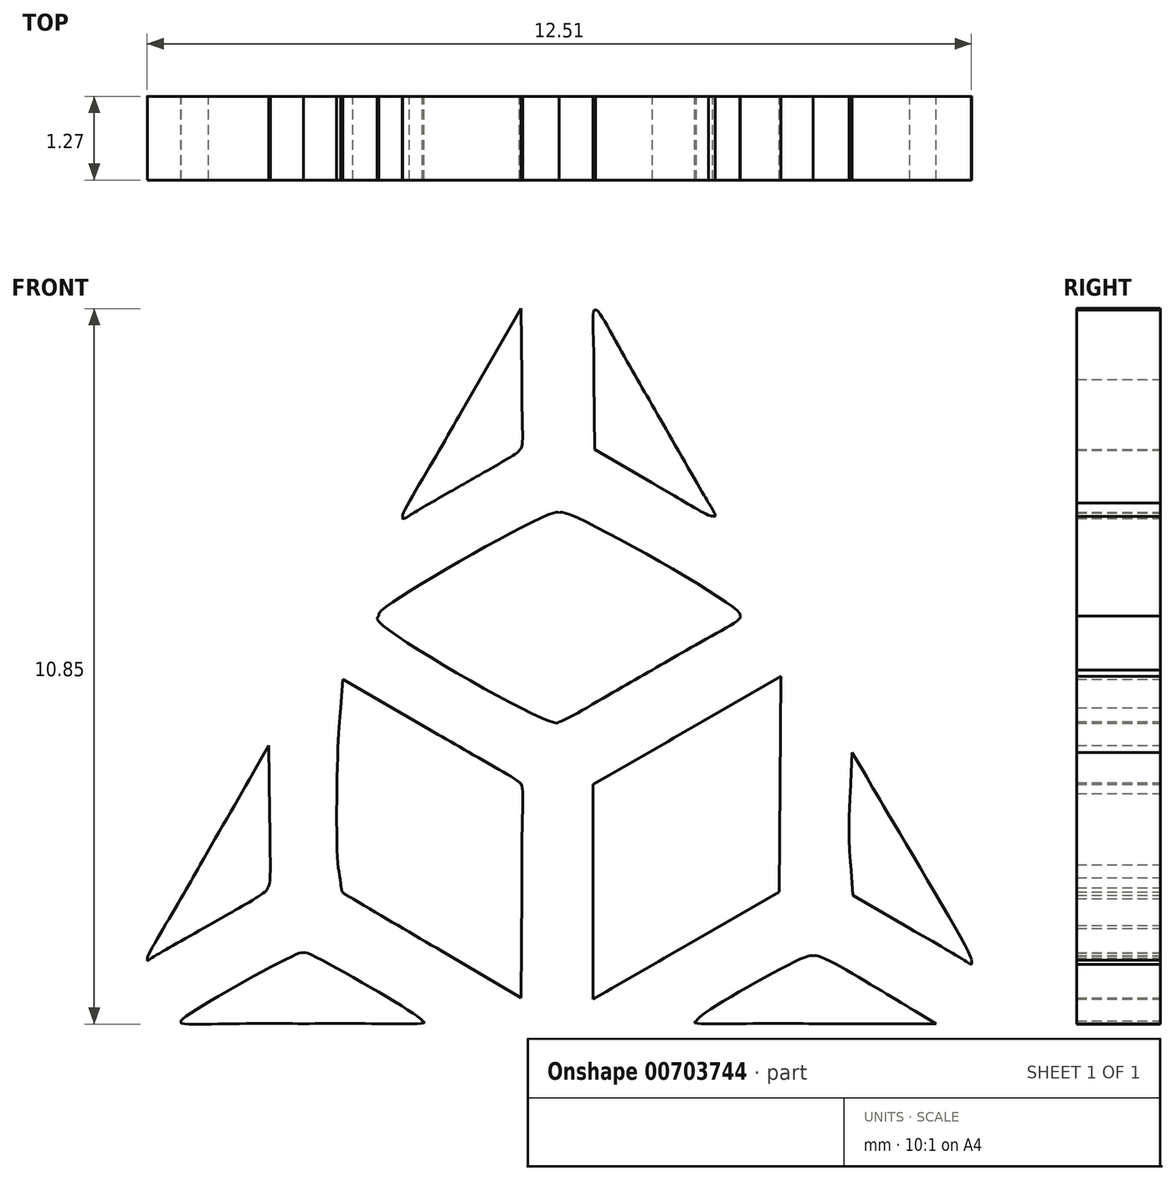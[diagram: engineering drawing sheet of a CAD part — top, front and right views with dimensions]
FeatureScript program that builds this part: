
annotation { "Feature Type Name" : "Feature", "Feature Type Description" : "" }
export const myFeature = defineFeature(function(context is Context, id is Id, definition is map)
    precondition{}
    {
        {
            var Q0;
            Q0=qCreatedBy(makeId("Front.planeOp"),FACE);
            var sketch = newSketch(context, id + "F0", { "sketchPlane" : qUnion([Q0])});
            skFitSpline(sketch, "E0", {"points": [v(-7.56, -9.6) * mm, v(-7.82, -9.54) * mm, v(-7.9, -9.44) * mm, v(-7.9, -9.18) * mm]});
            skFitSpline(sketch, "E1", {"points": [v(-7.9, -9.18) * mm, v(-7.89, -8.9) * mm, v(-8.03, -9.18) * mm, v(-5.89, -5.46) * mm]});
            skFitSpline(sketch, "E2", {"points": [v(-5.89, -5.46) * mm, v(-4.98, -3.9) * mm, v(-3.48, -1.3) * mm, v(-2.55, 0.32) * mm]});
            skFitSpline(sketch, "E3", {"points": [v(-2.55, 0.32) * mm, v(0.18, 5.07) * mm, v(0.04, 4.84) * mm, v(0.3, 4.9) * mm]});
            skFitSpline(sketch, "E4", {"points": [v(0.3, 4.9) * mm, v(0.37, 4.9) * mm, v(0.5, 4.9) * mm, v(0.57, 4.87) * mm]});
            skFitSpline(sketch, "E5", {"points": [v(0.57, 4.87) * mm, v(0.72, 4.82) * mm, v(0.6, 5.03) * mm, v(4.94, -2.5) * mm]});
            skFitSpline(sketch, "E6", {"points": [v(4.94, -2.5) * mm, v(8.66, -8.94) * mm, v(8.66, -8.95) * mm, v(8.68, -9.15) * mm]});
            skFitSpline(sketch, "E7", {"points": [v(8.68, -9.15) * mm, v(8.7, -9.4) * mm, v(8.64, -9.53) * mm, v(8.42, -9.59) * mm]});
            skFitSpline(sketch, "E8", {"points": [v(8.42, -9.59) * mm, v(8.22, -9.64) * mm, v(-7.27, -9.65) * mm, v(-7.56, -9.6) * mm]});
            skFitSpline(sketch, "E9", {"points": [v(-1.7, -8.52) * mm, v(-1.77, -8.45) * mm, v(-3.45, -7.5) * mm, v(-3.5, -7.5) * mm]});
            skFitSpline(sketch, "E10", {"points": [v(-3.5, -7.5) * mm, v(-3.55, -7.5) * mm, v(-5.35, -8.52) * mm, v(-5.35, -8.55) * mm]});
            skFitSpline(sketch, "E11", {"points": [v(-5.35, -8.55) * mm, v(-5.35, -8.56) * mm, v(-4.52, -8.56) * mm, v(-3.5, -8.56) * mm]});
            skFitSpline(sketch, "E12", {"points": [v(-3.5, -8.56) * mm, v(-2.41, -8.56) * mm, v(-1.67, -8.55) * mm, v(-1.7, -8.52) * mm]});
            skLineSegment(sketch, "E13", {"start": v(-7.56, -9.6) * mm, "end": v(-7.56, -9.6) * mm});
            skFitSpline(sketch, "E14", {"points": [v(5.85, -8.4) * mm, v(5.13, -7.98) * mm, v(4.32, -7.54) * mm, v(4.24, -7.54) * mm]});
            skFitSpline(sketch, "E15", {"points": [v(4.24, -7.54) * mm, v(4.16, -7.54) * mm, v(2.58, -8.42) * mm, v(2.47, -8.52) * mm]});
            skFitSpline(sketch, "E16", {"points": [v(2.47, -8.52) * mm, v(2.44, -8.55) * mm, v(3.17, -8.56) * mm, v(4.26, -8.56) * mm]});
            skFitSpline(sketch, "E17", {"points": [v(-0.22, -4.9) * mm, v(-0.24, -4.88) * mm, v(-0.86, -4.52) * mm, v(-1.58, -4.1) * mm]});
            skLineSegment(sketch, "E18", {"start": v(4.26, -8.56) * mm, "end": v(6.1, -8.56) * mm});
            skLineSegment(sketch, "E19", {"start": v(6.1, -8.56) * mm, "end": v(5.85, -8.4) * mm});
            skLineSegment(sketch, "E20", {"start": v(5.85, -8.4) * mm, "end": v(5.85, -8.4) * mm});
            skFitSpline(sketch, "E21", {"points": [v(-2.93, -3.77) * mm, v(-2.97, -4.36) * mm, v(-2.98, -6.07) * mm, v(-2.94, -6.35) * mm]});
            skFitSpline(sketch, "E22", {"points": [v(-2.94, -6.35) * mm, v(-2.92, -6.54) * mm, v(-2.89, -6.58) * mm, v(-2.75, -6.67) * mm]});
            skFitSpline(sketch, "E23", {"points": [v(-2.75, -6.67) * mm, v(-2.66, -6.72) * mm, v(-2.05, -7.08) * mm, v(-1.39, -7.47) * mm]});
            skLineSegment(sketch, "E24", {"start": v(-1.58, -4.1) * mm, "end": v(-2.9, -3.34) * mm});
            skLineSegment(sketch, "E25", {"start": v(-2.9, -3.34) * mm, "end": v(-2.93, -3.77) * mm});
            skFitSpline(sketch, "E26", {"points": [v(-0.18, -6.56) * mm, v(-0.18, -5.56) * mm, v(-0.19, -4.94) * mm, v(-0.22, -4.9) * mm]});
            skLineSegment(sketch, "E27", {"start": v(-1.39, -7.47) * mm, "end": v(-0.2, -8.17) * mm});
            skLineSegment(sketch, "E28", {"start": v(-0.2, -8.17) * mm, "end": v(-0.18, -6.56) * mm});
            skFitSpline(sketch, "E29", {"points": [v(2.57, -3.97) * mm, v(1.92, -4.35) * mm, v(1.28, -4.72) * mm, v(1.15, -4.8) * mm]});
            skLineSegment(sketch, "E30", {"start": v(2.51, -7.26) * mm, "end": v(3.72, -6.56) * mm});
            skLineSegment(sketch, "E31", {"start": v(3.72, -6.56) * mm, "end": v(3.74, -4.93) * mm});
            skLineSegment(sketch, "E32", {"start": v(3.74, -4.93) * mm, "end": v(3.75, -3.3) * mm});
            skLineSegment(sketch, "E33", {"start": v(3.75, -3.3) * mm, "end": v(2.57, -3.97) * mm});
            skFitSpline(sketch, "E34", {"points": [v(1.1, -8.08) * mm, v(1.2, -8.01) * mm, v(1.84, -7.65) * mm, v(2.51, -7.26) * mm]});
            skLineSegment(sketch, "E35", {"start": v(1.15, -4.8) * mm, "end": v(0.9, -4.93) * mm});
            skLineSegment(sketch, "E36", {"start": v(0.9, -4.93) * mm, "end": v(0.9, -6.56) * mm});
            skLineSegment(sketch, "E37", {"start": v(0.9, -6.56) * mm, "end": v(0.9, -8.2) * mm});
            skLineSegment(sketch, "E38", {"start": v(0.9, -8.2) * mm, "end": v(1.1, -8.08) * mm});
            skFitSpline(sketch, "E39", {"points": [v(6.64, -7.6) * mm, v(6.64, -7.58) * mm, v(5.53, -5.63) * mm, v(5, -4.75) * mm]});
            skFitSpline(sketch, "E40", {"points": [v(4.8, -5.07) * mm, v(4.79, -5.41) * mm, v(4.79, -5.9) * mm, v(4.8, -6.15) * mm]});
            skLineSegment(sketch, "E41", {"start": v(5, -4.75) * mm, "end": v(4.83, -4.45) * mm});
            skLineSegment(sketch, "E42", {"start": v(4.83, -4.45) * mm, "end": v(4.8, -5.07) * mm});
            skFitSpline(sketch, "E43", {"points": [v(5.7, -7.12) * mm, v(6.55, -7.62) * mm, v(6.64, -7.66) * mm, v(6.64, -7.6) * mm]});
            skLineSegment(sketch, "E44", {"start": v(4.8, -6.15) * mm, "end": v(4.84, -6.61) * mm});
            skLineSegment(sketch, "E45", {"start": v(4.84, -6.61) * mm, "end": v(5.7, -7.12) * mm});
            skFitSpline(sketch, "E46", {"points": [v(-4.94, -7.07) * mm, v(-4.47, -6.8) * mm, v(-4.07, -6.55) * mm, v(-4.04, -6.5) * mm]});
            skFitSpline(sketch, "E47", {"points": [v(-4.04, -6.5) * mm, v(-4.02, -6.46) * mm, v(-4, -5.97) * mm, v(-4, -5.38) * mm]});
            skFitSpline(sketch, "E48", {"points": [v(-4.14, -4.55) * mm, v(-4.2, -4.67) * mm, v(-4.62, -5.39) * mm, v(-5.06, -6.15) * mm]});
            skFitSpline(sketch, "E49", {"points": [v(-5.06, -6.15) * mm, v(-5.5, -6.92) * mm, v(-5.86, -7.55) * mm, v(-5.86, -7.57) * mm]});
            skFitSpline(sketch, "E50", {"points": [v(-5.86, -7.57) * mm, v(-5.86, -7.6) * mm, v(-5.84, -7.59) * mm, v(-4.94, -7.07) * mm]});
            skLineSegment(sketch, "E51", {"start": v(-4, -5.38) * mm, "end": v(-4.02, -4.34) * mm});
            skLineSegment(sketch, "E52", {"start": v(-4.02, -4.34) * mm, "end": v(-4.14, -4.55) * mm});
            skFitSpline(sketch, "E53", {"points": [v(1.8, -3.2) * mm, v(2.54, -2.77) * mm, v(3.13, -2.4) * mm, v(3.12, -2.38) * mm]});
            skFitSpline(sketch, "E54", {"points": [v(3.12, -2.38) * mm, v(3.1, -2.31) * mm, v(0.48, -0.82) * mm, v(0.38, -0.82) * mm]});
            skFitSpline(sketch, "E55", {"points": [v(0.38, -0.82) * mm, v(0.29, -0.82) * mm, v(-2.33, -2.32) * mm, v(-2.35, -2.38) * mm]});
            skFitSpline(sketch, "E56", {"points": [v(-2.35, -2.38) * mm, v(-2.37, -2.44) * mm, v(0.3, -4) * mm, v(0.39, -3.98) * mm]});
            skFitSpline(sketch, "E57", {"points": [v(0.39, -3.98) * mm, v(0.43, -3.97) * mm, v(1.06, -3.62) * mm, v(1.8, -3.2) * mm]});
            skFitSpline(sketch, "E58", {"points": [v(-1.03, -0.36) * mm, v(-0.61, -0.12) * mm, v(-0.25, 0.1) * mm, v(-0.22, 0.14) * mm]});
            skFitSpline(sketch, "E59", {"points": [v(-0.22, 0.14) * mm, v(-0.19, 0.18) * mm, v(-0.18, 0.55) * mm, v(-0.18, 1.24) * mm]});
            skFitSpline(sketch, "E60", {"points": [v(-1.1, 0.73) * mm, v(-1.59, -0.13) * mm, v(-2, -0.85) * mm, v(-2, -0.88) * mm]});
            skFitSpline(sketch, "E61", {"points": [v(-2, -0.88) * mm, v(-2, -0.9) * mm, v(-1.95, -0.9) * mm, v(-1.89, -0.86) * mm]});
            skFitSpline(sketch, "E62", {"points": [v(-1.89, -0.86) * mm, v(-1.83, -0.82) * mm, v(-1.44, -0.6) * mm, v(-1.03, -0.36) * mm]});
            skLineSegment(sketch, "E63", {"start": v(-0.18, 1.24) * mm, "end": v(-0.2, 2.28) * mm});
            skLineSegment(sketch, "E64", {"start": v(-0.2, 2.28) * mm, "end": v(-1.1, 0.73) * mm});
            skFitSpline(sketch, "E65", {"points": [v(2.65, -0.67) * mm, v(2.59, -0.56) * mm, v(2.18, 0.14) * mm, v(1.75, 0.9) * mm]});
            skFitSpline(sketch, "E66", {"points": [v(1.75, 0.9) * mm, v(1.32, 1.65) * mm, v(0.95, 2.26) * mm, v(0.93, 2.26) * mm]});
            skFitSpline(sketch, "E67", {"points": [v(0.93, 2.26) * mm, v(0.91, 2.26) * mm, v(0.9, 1.79) * mm, v(0.91, 1.2) * mm]});
            skFitSpline(sketch, "E68", {"points": [v(1.79, -0.36) * mm, v(2.26, -0.63) * mm, v(2.68, -0.86) * mm, v(2.71, -0.86) * mm]});
            skFitSpline(sketch, "E69", {"points": [v(2.71, -0.86) * mm, v(2.75, -0.86) * mm, v(2.73, -0.8) * mm, v(2.65, -0.67) * mm]});
            skLineSegment(sketch, "E70", {"start": v(0.91, 1.2) * mm, "end": v(0.92, 0.15) * mm});
            skLineSegment(sketch, "E71", {"start": v(0.92, 0.15) * mm, "end": v(1.79, -0.36) * mm});
            skSolve(sketch);
        }
        {
            var Q0;
            Q0=qSketchRegion(id+"F0",true);
            extrude(context, id + "F1", {"entities" : qUnion([Q0]), "depth" : 1.27 * mm, "offsetDistance" : 25.4 * mm});
        }
    });
